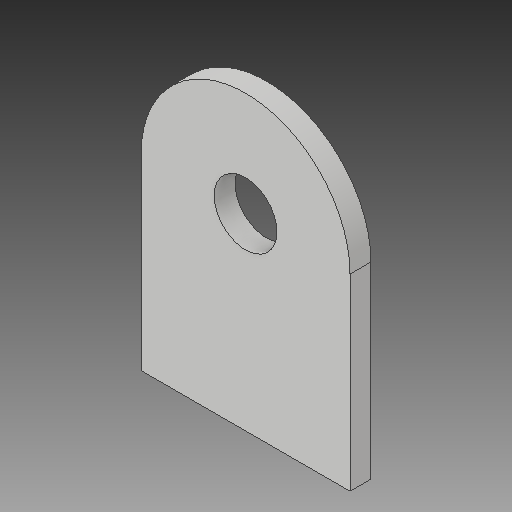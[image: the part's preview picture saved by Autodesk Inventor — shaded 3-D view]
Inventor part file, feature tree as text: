
AUTODESK INVENTOR PART (.ipt)
format: ipt  version: 2019 (Build 230136000, 136)  size: 107,008 bytes
history: native  units: mm
features: other x1, sketch x1, extrude x1, fillet x1, hole x1
ambient origin geometry x8: Origin, YZ Plane, XZ Plane, XY Plane, X Axis, Y Axis, Z Axis, Center Point
bodies: Body1 (feature_tree)
feature tree (5):
  other  "Bryła1"
  sketch  "Szkic1"
  extrude  "Wyciągnięcie proste1"  Depth=10.0mm
  fillet  "Zaokrąglenie1"  Radius=1.0mm
  hole  "Otwór1"  [1 undecoded]
note: 1 required parameter value undecoded (feature->parameter linkage not recoverable at this tier; creation-order binding heuristic only, values carry confidence <= 0.55)
